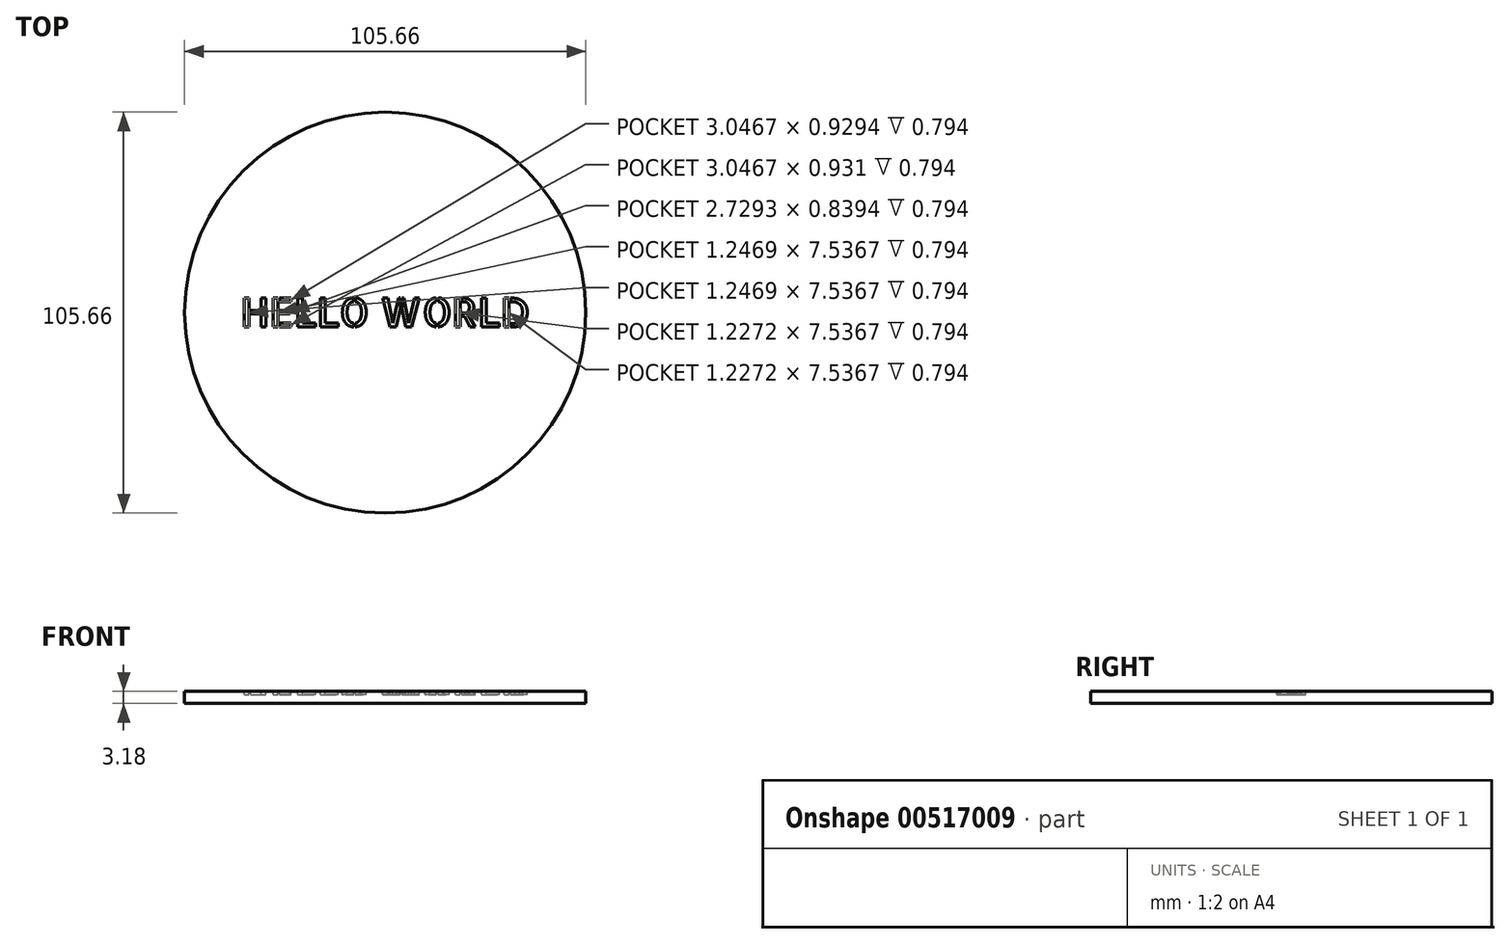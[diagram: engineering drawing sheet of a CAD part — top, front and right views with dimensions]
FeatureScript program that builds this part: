
annotation { "Feature Type Name" : "Feature", "Feature Type Description" : "" }
export const myFeature = defineFeature(function(context is Context, id is Id, definition is map)
    precondition{}
    {
        {
            var Q0;
            Q0=qCreatedBy(makeId("Top.planeOp"),FACE);
            var sketch = newSketch(context, id + "F0", { "sketchPlane" : qUnion([Q0])});
            skCircle(sketch, "E0", {"center": v(0, 0) * mm, "radius": 52.83 * mm});
            skSolve(sketch);
        }
        {
            var Q0;
            Q0 = qSketchRegion(id + "F0", true);
            extrude(context, id + "F1", {"entities" : qUnion([Q0]), "endBound" : BoundingType.SYMMETRIC, "depth" : 3.17 * mm, "offsetDistance" : 25.4 * mm});
        }
        {
            var Q0;
            Q0=makeQuery(id+"F1.opExtrude","CAP_FACE",FACE,{"disambiguationData":[OSD([sQuery(id+"F0.wireOp",EDGE,"E0")])],"isStart":false});
            var sketch = newSketch(context, id + "F2", { "sketchPlane" : qUnion([Q0])});
            skText(sketch, "E1", { "text": "HELLO WORLD", "fontName": "AllertaStencil-Regular.ttf"});
            const initialGuessF2  = {"E1": [-0.0381, -0.00373, 1, 0, 0.00754]};
            skSetInitialGuess(sketch, initialGuessF2);
            skSolve(sketch);
        }
        {
            var Q0;
            Q0 = qSketchRegion(id + "F2", true);
            extrude(context, id + "F3", {"entities" : qUnion([Q0]), "operationType" : NewBodyOperationType.REMOVE, "oppositeDirection" : true, "depth" : 0.8 * mm, "offsetDistance" : 25.4 * mm});
        }
    });
